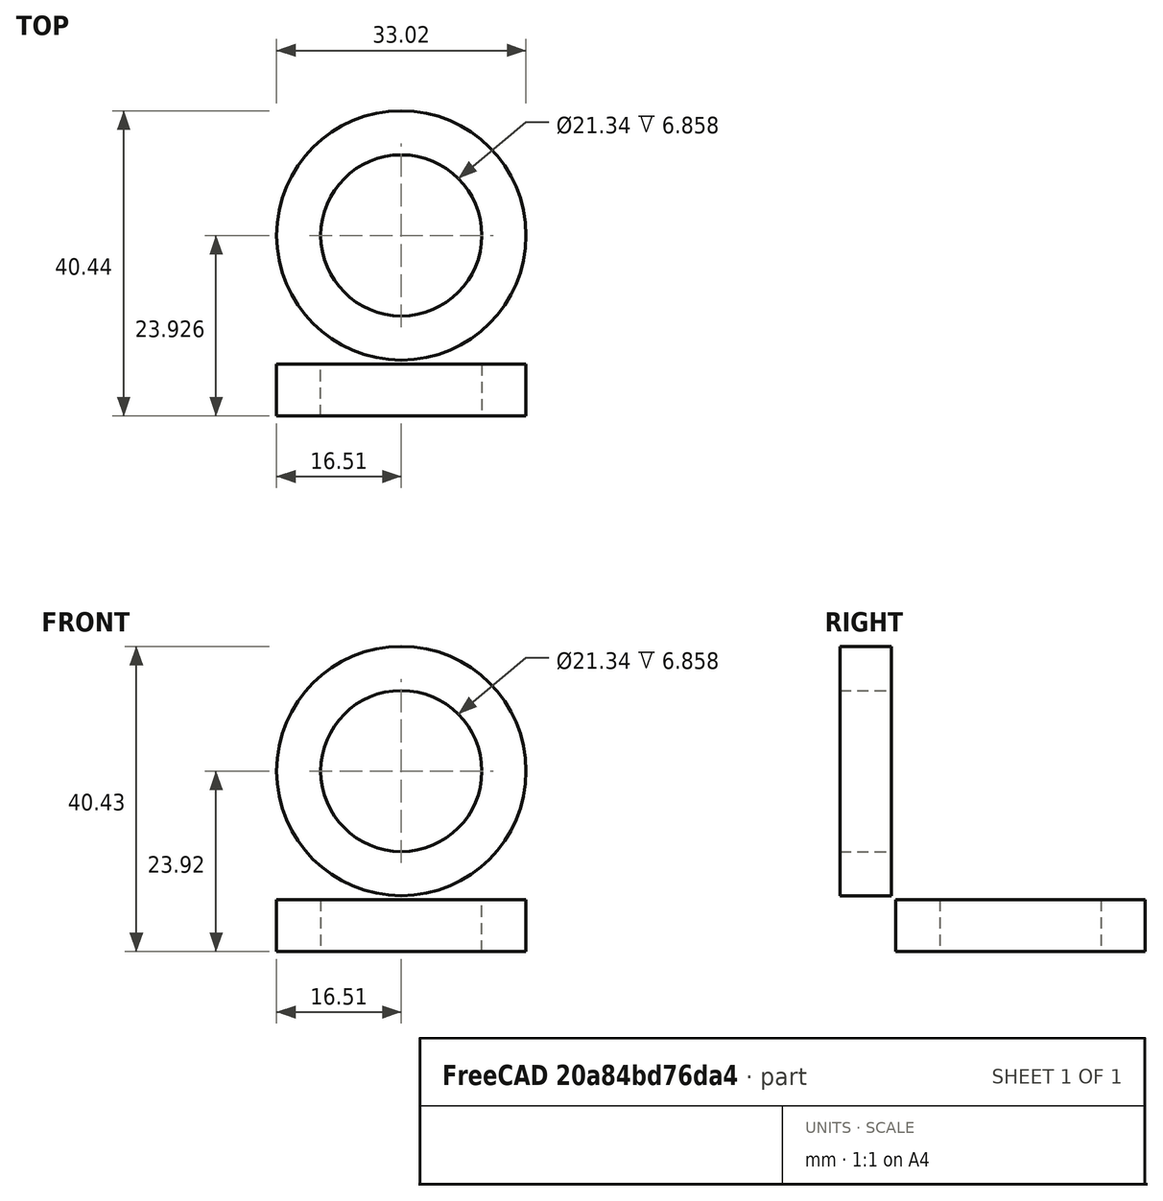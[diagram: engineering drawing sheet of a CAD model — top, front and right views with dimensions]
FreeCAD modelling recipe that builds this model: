
FCSTD DOCUMENT  (FreeCAD 0.16R6712 (Git))
Label: 0.5in NPT 90 elbow
License: CreativeCommons Attribution-ShareAlike
LicenseURL: http://creativecommons.org/licenses/by-sa/4.0/
objects: Part::FeaturePython×4, Part::Circle×3, App::FeaturePython×3, Part::Sweep×2, Sketcher::SketchObject×1, PartDesign::Pad×1
note: 12 computed .brp shape members not serialized (recipe doc carries the construction recipe); baked Part::Feature solids carry a one-line shape summary decoded from their .brp

FEATURE [Part::Circle] Base  label="ID"
  Angle0 = 0
  Angle1 = 360
  Placement = pos=(0,0,-17.0656) rot=(0,0,1;0rad)
  Radius = 10.668
FEATURE [Part::Circle] Trajectory  label="Trajectory 90 elbow"
  Angle0 = 90
  Angle1 = 180
  Placement = pos=(17.0656,0,-17.0656) rot=(1,0,0;1.5708rad)
  Radius = 17.0656
FEATURE [Part::Sweep] Sweep  label="inner"
  Frenet = false
  Sections = -> [Base]
  Solid = false
  Spine = -> Trajectory
  Transition = 1
FEATURE [Part::Circle] Base001  label="OD"
  Angle0 = 0
  Angle1 = 360
  Placement = pos=(0,0,-17.0656) rot=(0,0,1;0rad)
  Radius = 15.24
FEATURE [Part::Sweep] Sweep001  label="outer"
  Frenet = false
  Sections = -> [Base001]
  Solid = false
  Spine = -> Trajectory [Edge1]
  Transition = 1
FEATURE [Sketcher::SketchObject] Sketch002  label="thread end "
  Placement = pos=(50.8,-127,0) rot=(1,0,0;1.5708rad)
  sketch-geometry (2):
    g0: Circle CenterX=0 CenterY=0 CenterZ=0 NormalX=0 NormalY=0 NormalZ=1 Radius=10.668
    g1: Circle CenterX=0 CenterY=0 CenterZ=0 NormalX=0 NormalY=0 NormalZ=1 Radius=16.51
  constraints (4):
    c: Coincident(g0,g-1)
    c: Radius(g0) = 10.668
    c: Coincident(g1,g-1)
    c: Radius(g1) = 16.51
FEATURE [PartDesign::Pad] Pad  label="End"
  Length = 6.858
  Length2 = 100
  Placement = pos=(50.8,-127,0) rot=(1,0,0;1.5708rad)
  Sketch = -> Sketch002
  Type = 0
FEATURE [Part::FeaturePython] Clone  label="Clone of outer"  # Draft clone (typed FeaturePython)
  Objects = -> [Sweep001]
  Placement = pos=(0,-236.934,0) rot=(0,0,-1;1.5708rad)
  Scale = (1,1,1)
FEATURE [Part::FeaturePython] Clone001  label="Clone of inner"  # Draft clone (typed FeaturePython)
  Objects = -> [Sweep]
  Placement = pos=(0,-236.934,0) rot=(0,0,-1;1.5708rad)
  Scale = (1,1,1)
FEATURE [Part::FeaturePython] Clone002  label="Clone of End"  # Draft clone (typed FeaturePython)
  Objects = -> [Pad]
  Placement = pos=(0,-254,0) rot=(1,0,0;1.5708rad)
  Scale = (1,1,1)
FEATURE [Part::FeaturePython] Clone003  label="Clone of End001"  # Draft clone (typed FeaturePython)
  Objects = -> [Pad]
  Placement = pos=(0,-236.934,-23.9236) rot=(0,0,1;0rad)
  Scale = (1,1,1)
FEATURE [App::FeaturePython] circularEdgeConstraint01  # a2plus constraint (typed FeaturePython)
  Object1 = Clone002
  Object2 = Clone001
  SubElement1 = Edge5
  SubElement2 = Edge2
  Type = circularEdge
  directionConstraint = 0
  lockRotation = false
  offset = 0
FEATURE [App::FeaturePython] circularEdgeConstraint02  # a2plus constraint (typed FeaturePython)
  Object1 = Clone
  Object2 = Clone002
  SubElement1 = Edge2
  SubElement2 = Edge2
  Type = circularEdge
  directionConstraint = 0
  lockRotation = false
  offset = 0
FEATURE [App::FeaturePython] circularEdgeConstraint03  # a2plus constraint (typed FeaturePython)
  Object1 = Clone003
  Object2 = Clone001
  SubElement1 = Edge6
  SubElement2 = Edge3
  Type = circularEdge
  directionConstraint = 0
  lockRotation = false
  offset = 0
